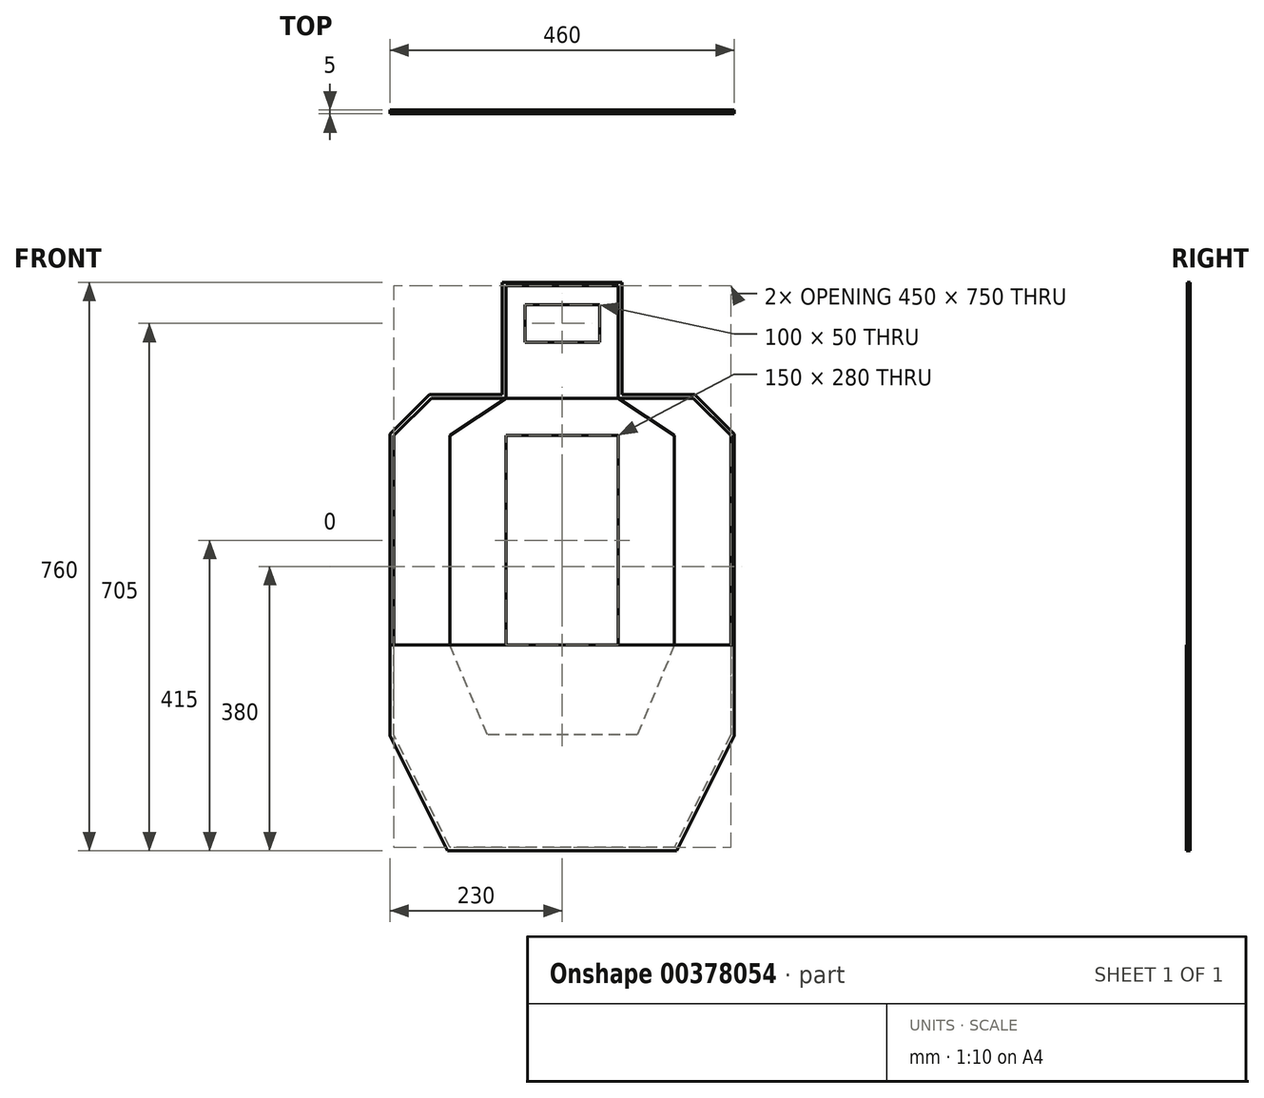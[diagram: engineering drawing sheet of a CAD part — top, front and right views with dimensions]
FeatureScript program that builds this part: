
annotation { "Feature Type Name" : "Feature", "Feature Type Description" : "" }
export const myFeature = defineFeature(function(context is Context, id is Id, definition is map)
    precondition{}
    {
        {
            var Q0;
            Q0=qCreatedBy(makeId("Front.planeOp"),FACE);
            var sketch = newSketch(context, id + "F0", { "sketchPlane" : qUnion([Q0])});
            skLineSegment(sketch, "E0.bottom", {"start": v(0, 100) * mm, "end": v(50, 100) * mm, "construction": true});
            skLineSegment(sketch, "E0.top", {"start": v(0, 125) * mm, "end": v(50, 125) * mm});
            skLineSegment(sketch, "E0.right", {"start": v(50, 100) * mm, "end": v(50, 125) * mm});
            skLineSegment(sketch, "E1.MirrorCS", {"start": v(0, 75) * mm, "end": v(50, 75) * mm});
            skLineSegment(sketch, "E2.MirrorCS", {"start": v(50, 100) * mm, "end": v(50, 75) * mm});
            skLineSegment(sketch, "E3.MirrorCS", {"start": v(0, 0) * mm, "end": v(0, 100) * mm, "construction": true});
            skLineSegment(sketch, "E4.MirrorCS", {"start": v(0, 125) * mm, "end": v(-50, 125) * mm});
            skLineSegment(sketch, "E5.MirrorCS", {"start": v(-50, 100) * mm, "end": v(-50, 125) * mm});
            skLineSegment(sketch, "E6.MirrorCS", {"start": v(-50, 100) * mm, "end": v(-50, 75) * mm});
            skLineSegment(sketch, "E7.MirrorCS", {"start": v(0, 75) * mm, "end": v(-50, 75) * mm});
            skSolve(sketch);
        }
        {
            var Q0;
            Q0=qSketchRegion(id+"F0",true);
            extrude(context, id + "F1", {"entities" : qUnion([Q0]), "oppositeDirection" : true, "depth" : 3 * mm});
        }
        {
            var Q0;
            Q0=qCreatedBy(makeId("Front.planeOp"),FACE);
            var sketch = newSketch(context, id + "F2", { "sketchPlane" : qUnion([Q0])});
            skLineSegment(sketch, "E8", {"start": v(75, 0) * mm, "end": v(75, 150) * mm});
            skLineSegment(sketch, "E9", {"start": v(75, 150) * mm, "end": v(-75, 150) * mm});
            skLineSegment(sketch, "E10", {"start": v(-75, 150) * mm, "end": v(-75, 0) * mm});
            skLineSegment(sketch, "E11", {"start": v(-75, 0) * mm, "end": v(75, 0) * mm});
            skLineSegment(sketch, "E12.0", {"start": v(0, 125) * mm, "end": v(-50, 125) * mm});
            skLineSegment(sketch, "E13.0", {"start": v(0, 125) * mm, "end": v(50, 125) * mm});
            skLineSegment(sketch, "E14.0", {"start": v(50, 100) * mm, "end": v(50, 125) * mm});
            skLineSegment(sketch, "E15.1", {"start": v(50, 100) * mm, "end": v(50, 75) * mm});
            skLineSegment(sketch, "E16.0", {"start": v(0, 75) * mm, "end": v(50, 75) * mm});
            skLineSegment(sketch, "E17.0", {"start": v(0, 75) * mm, "end": v(-50, 75) * mm});
            skLineSegment(sketch, "E18.0", {"start": v(-50, 100) * mm, "end": v(-50, 75) * mm});
            skLineSegment(sketch, "E19.1", {"start": v(-50, 100) * mm, "end": v(-50, 125) * mm});
            skLineSegment(sketch, "E20", {"start": v(0, 125) * mm, "end": v(0, 150) * mm, "construction": true});
            skLineSegment(sketch, "E21", {"start": v(0, 150) * mm, "end": v(0, 137.5) * mm, "construction": true});
            skSolve(sketch);
        }
        {
            var Q0;
            {var subQ0=sQuery(id+"F2.wireOp",EDGE,"E8");Q0=makeQuery(id+"F2.imprint","IMPRINT",FACE,{"disambiguationData":[TD([[makeQuery(id+"F2.imprint","IMPRINT",EDGE,{"derivedFrom":subQ0}),1.0]])]});}
            extrude(context, id + "F3", {"entities" : qUnion([Q0]), "oppositeDirection" : true, "depth" : 3 * mm});
        }
        {
            var Q0;
            Q0=qCreatedBy(makeId("Front.planeOp"),FACE);
            var sketch = newSketch(context, id + "F4", { "sketchPlane" : qUnion([Q0])});
            skLineSegment(sketch, "E22.bottom", {"start": v(75, -50) * mm, "end": v(-75, -50) * mm});
            skLineSegment(sketch, "E22.top", {"start": v(75, -330) * mm, "end": v(-75, -330) * mm});
            skLineSegment(sketch, "E22.left", {"start": v(75, -50) * mm, "end": v(75, -330) * mm});
            skLineSegment(sketch, "E22.right", {"start": v(-75, -50) * mm, "end": v(-75, -330) * mm});
            skLineSegment(sketch, "E23", {"start": v(0, 0) * mm, "end": v(0, -50) * mm, "construction": true});
            skLineSegment(sketch, "E24.0", {"start": v(-75, 0) * mm, "end": v(75, 0) * mm, "construction": true});
            skLineSegment(sketch, "E25", {"start": v(75, 0) * mm, "end": v(75, -50) * mm, "construction": true});
            skSolve(sketch);
        }
        {
            var Q0;
            Q0=makeQuery(id+"F4.imprint","IMPRINT",FACE,{"disambiguationData":[TD([[makeQuery(id+"F4.imprint","IMPRINT",EDGE,{"derivedFrom":sQuery(id+"F4.wireOp",EDGE,"E22.bottom")}),1.0]])]});
            extrude(context, id + "F5", {"entities" : qUnion([Q0]), "oppositeDirection" : true, "depth" : 3 * mm});
        }
        {
            var Q0;
            Q0=qCreatedBy(makeId("Front.planeOp"),FACE);
            var sketch = newSketch(context, id + "F6", { "sketchPlane" : qUnion([Q0])});
            skLineSegment(sketch, "E26.0", {"start": v(-75, 0) * mm, "end": v(75, 0) * mm});
            skLineSegment(sketch, "E27.1", {"start": v(75, -50) * mm, "end": v(75, -330) * mm});
            skLineSegment(sketch, "E28.2", {"start": v(75, -50) * mm, "end": v(-75, -50) * mm});
            skLineSegment(sketch, "E29.3", {"start": v(-75, -50) * mm, "end": v(-75, -330) * mm});
            skLineSegment(sketch, "E30.0", {"start": v(75, -330) * mm, "end": v(-75, -330) * mm});
            skLineSegment(sketch, "E31", {"start": v(75, 0) * mm, "end": v(150, -50) * mm});
            skLineSegment(sketch, "E32", {"start": v(150, -50) * mm, "end": v(150, -330) * mm});
            skLineSegment(sketch, "E33", {"start": v(150, -330) * mm, "end": v(100, -450) * mm});
            skLineSegment(sketch, "E34", {"start": v(100, -450) * mm, "end": v(-100, -450) * mm});
            skLineSegment(sketch, "E35", {"start": v(-100, -450) * mm, "end": v(-150, -330) * mm});
            skLineSegment(sketch, "E36", {"start": v(-150, -330) * mm, "end": v(-150, -50) * mm});
            skLineSegment(sketch, "E37", {"start": v(-150, -50) * mm, "end": v(-75, 0) * mm});
            skLineSegment(sketch, "E38", {"start": v(0, -450) * mm, "end": v(0, -50) * mm, "construction": true});
            skLineSegment(sketch, "E39", {"start": v(150, -50) * mm, "end": v(75, -50) * mm, "construction": true});
            skLineSegment(sketch, "E40", {"start": v(-55.04, -50) * mm, "end": v(-150, -50) * mm, "construction": true});
            skLineSegment(sketch, "E41", {"start": v(150, -330) * mm, "end": v(150, -450) * mm, "construction": true});
            skLineSegment(sketch, "E42", {"start": v(100, -450) * mm, "end": v(150, -450) * mm, "construction": true});
            skLineSegment(sketch, "E43", {"start": v(150, -330) * mm, "end": v(-150, -330) * mm, "construction": true});
            skLineSegment(sketch, "E44", {"start": v(-150, -330) * mm, "end": v(-150, -450) * mm, "construction": true});
            skLineSegment(sketch, "E45", {"start": v(-150, -450) * mm, "end": v(-100, -450) * mm, "construction": true});
            skSolve(sketch);
        }
        {
            var Q0;
            Q0=makeQuery(id+"F6.imprint","IMPRINT",FACE,{"disambiguationData":[TD([[makeQuery(id+"F6.imprint","IMPRINT",EDGE,{"derivedFrom":sQuery(id+"F6.wireOp",EDGE,"E26.0")}),-1.0]])]});
            extrude(context, id + "F7", {"entities" : qUnion([Q0]), "oppositeDirection" : true, "depth" : 3 * mm});
        }
        {
            var Q0;
            Q0=makeQuery(id+"F7.opExtrude","CAP_FACE",FACE,{"disambiguationData":[OSD([sQuery(id+"F6.wireOp",EDGE,"E26.0"),sQuery(id+"F6.wireOp",EDGE,"E27.1"),sQuery(id+"F6.wireOp",EDGE,"E28.2"),sQuery(id+"F6.wireOp",EDGE,"E29.3"),sQuery(id+"F6.wireOp",EDGE,"E30.0"),sQuery(id+"F6.wireOp",EDGE,"E31"),sQuery(id+"F6.wireOp",EDGE,"E32"),sQuery(id+"F6.wireOp",EDGE,"E33"),sQuery(id+"F6.wireOp",EDGE,"E34"),sQuery(id+"F6.wireOp",EDGE,"E35"),sQuery(id+"F6.wireOp",EDGE,"E36"),sQuery(id+"F6.wireOp",EDGE,"E37")])],"isStart":true});
            var sketch = newSketch(context, id + "F8", { "sketchPlane" : qUnion([Q0])});
            skLineSegment(sketch, "E46.0", {"start": v(75, 0) * mm, "end": v(150, -50) * mm});
            skLineSegment(sketch, "E47.0", {"start": v(150, -50) * mm, "end": v(150, -330) * mm});
            skLineSegment(sketch, "E48.0", {"start": v(150, -330) * mm, "end": v(100, -450) * mm});
            skLineSegment(sketch, "E49.1", {"start": v(100, -450) * mm, "end": v(-100, -450) * mm});
            skLineSegment(sketch, "E50.0", {"start": v(-150, -330) * mm, "end": v(-150, -50) * mm});
            skLineSegment(sketch, "E51.0", {"start": v(-100, -450) * mm, "end": v(-150, -330) * mm});
            skLineSegment(sketch, "E52.0", {"start": v(-150, -50) * mm, "end": v(-75, 0) * mm});
            skLineSegment(sketch, "E53", {"start": v(75, 0) * mm, "end": v(175, 0) * mm});
            skLineSegment(sketch, "E54", {"start": v(175, 0) * mm, "end": v(225, -50) * mm});
            skLineSegment(sketch, "E55", {"start": v(225, -50) * mm, "end": v(225, -450) * mm});
            skLineSegment(sketch, "E56", {"start": v(225, -450) * mm, "end": v(150, -600) * mm});
            skLineSegment(sketch, "E57", {"start": v(150, -600) * mm, "end": v(-150, -600) * mm});
            skLineSegment(sketch, "E58", {"start": v(-150, -600) * mm, "end": v(-225, -450) * mm});
            skLineSegment(sketch, "E59", {"start": v(-225, -450) * mm, "end": v(-225, -50) * mm});
            skLineSegment(sketch, "E60", {"start": v(-225, -50) * mm, "end": v(-175, 0) * mm});
            skLineSegment(sketch, "E61", {"start": v(-175, 0) * mm, "end": v(-75, 0) * mm});
            skLineSegment(sketch, "E62", {"start": v(225, -50) * mm, "end": v(225, 0) * mm, "construction": true});
            skLineSegment(sketch, "E63", {"start": v(225, 0) * mm, "end": v(175, 0) * mm, "construction": true});
            skLineSegment(sketch, "E64", {"start": v(225, -450) * mm, "end": v(225, -600) * mm, "construction": true});
            skLineSegment(sketch, "E65", {"start": v(225, -600) * mm, "end": v(150, -600) * mm, "construction": true});
            skLineSegment(sketch, "E66", {"start": v(-225, -450) * mm, "end": v(-225, -600) * mm, "construction": true});
            skLineSegment(sketch, "E67", {"start": v(-225, -600) * mm, "end": v(-150, -600) * mm, "construction": true});
            skLineSegment(sketch, "E68", {"start": v(-175, 0) * mm, "end": v(-225, 0) * mm, "construction": true});
            skLineSegment(sketch, "E69", {"start": v(-225, 0) * mm, "end": v(-225, -50) * mm, "construction": true});
            skSolve(sketch);
        }
        {
            var Q0;
            Q0=qSketchRegion(id+"F8",true);
            extrude(context, id + "F9", {"entities" : qUnion([Q0]), "oppositeDirection" : true, "depth" : 3 * mm});
        }
        {
            var Q0;
            Q0=makeQuery(id+"F9.opExtrude","CAP_FACE",FACE,{"disambiguationData":[OSD([sQuery(id+"F8.wireOp",EDGE,"E46.0"),sQuery(id+"F8.wireOp",EDGE,"E47.0"),sQuery(id+"F8.wireOp",EDGE,"E48.0"),sQuery(id+"F8.wireOp",EDGE,"E49.1"),sQuery(id+"F8.wireOp",EDGE,"E50.0"),sQuery(id+"F8.wireOp",EDGE,"E51.0"),sQuery(id+"F8.wireOp",EDGE,"E52.0"),sQuery(id+"F8.wireOp",EDGE,"E53"),sQuery(id+"F8.wireOp",EDGE,"E54"),sQuery(id+"F8.wireOp",EDGE,"E55"),sQuery(id+"F8.wireOp",EDGE,"E56"),sQuery(id+"F8.wireOp",EDGE,"E57"),sQuery(id+"F8.wireOp",EDGE,"E58"),sQuery(id+"F8.wireOp",EDGE,"E59"),sQuery(id+"F8.wireOp",EDGE,"E60"),sQuery(id+"F8.wireOp",EDGE,"E61")])],"isStart":true});
            var sketch = newSketch(context, id + "F10", { "sketchPlane" : qUnion([Q0])});
            skLineSegment(sketch, "E70.0", {"start": v(75, 150) * mm, "end": v(-75, 150) * mm});
            skLineSegment(sketch, "E71.0", {"start": v(75, 0) * mm, "end": v(75, 150) * mm});
            skLineSegment(sketch, "E72.1", {"start": v(75, 0) * mm, "end": v(175, 0) * mm});
            skLineSegment(sketch, "E73.0", {"start": v(175, 0) * mm, "end": v(225, -50) * mm});
            skLineSegment(sketch, "E74.1", {"start": v(225, -50) * mm, "end": v(225, -450) * mm});
            skLineSegment(sketch, "E75.0", {"start": v(225, -450) * mm, "end": v(150, -600) * mm});
            skLineSegment(sketch, "E76.1", {"start": v(150, -600) * mm, "end": v(-150, -600) * mm});
            skLineSegment(sketch, "E77.2", {"start": v(-150, -600) * mm, "end": v(-225, -450) * mm});
            skLineSegment(sketch, "E78.3", {"start": v(-225, -450) * mm, "end": v(-225, -50) * mm});
            skLineSegment(sketch, "E79.4", {"start": v(-225, -50) * mm, "end": v(-175, 0) * mm});
            skLineSegment(sketch, "E80.5", {"start": v(-175, 0) * mm, "end": v(-75, 0) * mm});
            skLineSegment(sketch, "E81.0", {"start": v(-75, 150) * mm, "end": v(-75, 0) * mm});
            skLineSegment(sketch, "E82.0", {"start": v(177.07, 5) * mm, "end": v(230, -47.93) * mm});
            skLineSegment(sketch, "E82.1", {"start": v(-230, -451.18) * mm, "end": v(-230, -47.93) * mm});
            skLineSegment(sketch, "E82.2", {"start": v(-153.1, -605) * mm, "end": v(-230, -451.18) * mm});
            skLineSegment(sketch, "E82.3", {"start": v(153.1, -605) * mm, "end": v(-153.1, -605) * mm});
            skLineSegment(sketch, "E82.4", {"start": v(230, -451.18) * mm, "end": v(153.1, -605) * mm});
            skLineSegment(sketch, "E82.5", {"start": v(-230, -47.93) * mm, "end": v(-177.07, 5) * mm});
            skLineSegment(sketch, "E82.6", {"start": v(230, -47.93) * mm, "end": v(230, -451.18) * mm});
            skLineSegment(sketch, "E82.7", {"start": v(-177.07, 5) * mm, "end": v(-80, 5) * mm});
            skLineSegment(sketch, "E82.8", {"start": v(-80, 155) * mm, "end": v(-80, 5) * mm});
            skLineSegment(sketch, "E82.9", {"start": v(80, 155) * mm, "end": v(-80, 155) * mm});
            skLineSegment(sketch, "E82.10", {"start": v(80, 5) * mm, "end": v(80, 155) * mm});
            skLineSegment(sketch, "E82.11", {"start": v(80, 5) * mm, "end": v(177.07, 5) * mm});
            skSolve(sketch);
        }
        {
            var Q0;
            Q0=makeQuery(id+"F10.imprint","IMPRINT",FACE,{"disambiguationData":[TD([[makeQuery(id+"F10.imprint","IMPRINT",EDGE,{"derivedFrom":sQuery(id+"F10.wireOp",EDGE,"E70.0")}),-1.0]])]});
            extrude(context, id + "F11", {"entities" : qUnion([Q0]), "oppositeDirection" : true, "depth" : 3 * mm});
        }
        {
            var Q0;
            Q0=makeQuery(id+"F9.opExtrude","CAP_FACE",FACE,{"disambiguationData":[OSD([sQuery(id+"F8.wireOp",EDGE,"E46.0"),sQuery(id+"F8.wireOp",EDGE,"E47.0"),sQuery(id+"F8.wireOp",EDGE,"E48.0"),sQuery(id+"F8.wireOp",EDGE,"E49.1"),sQuery(id+"F8.wireOp",EDGE,"E50.0"),sQuery(id+"F8.wireOp",EDGE,"E51.0"),sQuery(id+"F8.wireOp",EDGE,"E52.0"),sQuery(id+"F8.wireOp",EDGE,"E53"),sQuery(id+"F8.wireOp",EDGE,"E54"),sQuery(id+"F8.wireOp",EDGE,"E55"),sQuery(id+"F8.wireOp",EDGE,"E56"),sQuery(id+"F8.wireOp",EDGE,"E57"),sQuery(id+"F8.wireOp",EDGE,"E58"),sQuery(id+"F8.wireOp",EDGE,"E59"),sQuery(id+"F8.wireOp",EDGE,"E60"),sQuery(id+"F8.wireOp",EDGE,"E61")])],"isStart":false});
            var sketch = newSketch(context, id + "F12", { "sketchPlane" : qUnion([Q0])});
            skLineSegment(sketch, "E83.0", {"start": v(75, 150) * mm, "end": v(75, 0) * mm});
            skLineSegment(sketch, "E84.0", {"start": v(175, 0) * mm, "end": v(75, 0) * mm});
            skLineSegment(sketch, "E85.0", {"start": v(-75, 150) * mm, "end": v(75, 150) * mm});
            skLineSegment(sketch, "E86.0", {"start": v(225, -50) * mm, "end": v(175, 0) * mm});
            skLineSegment(sketch, "E87.0", {"start": v(-225, -50) * mm, "end": v(-225, -450) * mm});
            skLineSegment(sketch, "E87.1", {"start": v(225, -450) * mm, "end": v(225, -50) * mm});
            skLineSegment(sketch, "E87.2", {"start": v(150, -600) * mm, "end": v(225, -450) * mm});
            skLineSegment(sketch, "E87.3", {"start": v(-225, -450) * mm, "end": v(-150, -600) * mm});
            skLineSegment(sketch, "E87.4", {"start": v(-150, -600) * mm, "end": v(150, -600) * mm});
            skLineSegment(sketch, "E88.0", {"start": v(-175, 0) * mm, "end": v(-225, -50) * mm});
            skLineSegment(sketch, "E89.0", {"start": v(-75, 0) * mm, "end": v(-175, 0) * mm});
            skLineSegment(sketch, "E90.0", {"start": v(-75, 0) * mm, "end": v(-75, 150) * mm});
            skSolve(sketch);
        }
        {
            var Q0;
            Q0=qSketchRegion(id+"F12",true);
            extrude(context, id + "F13", {"entities" : qUnion([Q0]), "depth" : 1 * mm});
        }
        {
            var Q0;
            Q0=makeQuery(id+"F13.opExtrude","CAP_FACE",FACE,{"disambiguationData":[OSD([sQuery(id+"F12.wireOp",EDGE,"E83.0"),sQuery(id+"F12.wireOp",EDGE,"E84.0"),sQuery(id+"F12.wireOp",EDGE,"E85.0"),sQuery(id+"F12.wireOp",EDGE,"E86.0"),sQuery(id+"F12.wireOp",EDGE,"E87.0"),sQuery(id+"F12.wireOp",EDGE,"E87.1"),sQuery(id+"F12.wireOp",EDGE,"E87.2"),sQuery(id+"F12.wireOp",EDGE,"E87.3"),sQuery(id+"F12.wireOp",EDGE,"E87.4"),sQuery(id+"F12.wireOp",EDGE,"E88.0"),sQuery(id+"F12.wireOp",EDGE,"E89.0"),sQuery(id+"F12.wireOp",EDGE,"E90.0")])],"isStart":false});
            var sketch = newSketch(context, id + "F14", { "sketchPlane" : qUnion([Q0])});
            skLineSegment(sketch, "E91.0", {"start": v(-80, 155) * mm, "end": v(80, 155) * mm});
            skLineSegment(sketch, "E92.0", {"start": v(80, 155) * mm, "end": v(80, 5) * mm});
            skLineSegment(sketch, "E93.0", {"start": v(-80, 5) * mm, "end": v(-80, 155) * mm});
            skLineSegment(sketch, "E94.0", {"start": v(177.07, 5) * mm, "end": v(80, 5) * mm});
            skLineSegment(sketch, "E95.0", {"start": v(-80, 5) * mm, "end": v(-177.07, 5) * mm});
            skLineSegment(sketch, "E96.0", {"start": v(230, -47.93) * mm, "end": v(177.07, 5) * mm});
            skLineSegment(sketch, "E97.0", {"start": v(-177.07, 5) * mm, "end": v(-230, -47.93) * mm});
            skLineSegment(sketch, "E98.1", {"start": v(-230, -47.93) * mm, "end": v(-230, -451.18) * mm});
            skLineSegment(sketch, "E99.0", {"start": v(-230, -451.18) * mm, "end": v(-153.1, -605) * mm});
            skLineSegment(sketch, "E100.0", {"start": v(-153.1, -605) * mm, "end": v(153.1, -605) * mm});
            skLineSegment(sketch, "E101.0", {"start": v(153.1, -605) * mm, "end": v(230, -451.18) * mm});
            skLineSegment(sketch, "E102.0", {"start": v(230, -451.18) * mm, "end": v(230, -47.93) * mm});
            skLineSegment(sketch, "E103.0", {"start": v(-75, 150) * mm, "end": v(75, 150) * mm});
            skLineSegment(sketch, "E104.0", {"start": v(-75, 0) * mm, "end": v(-75, 150) * mm});
            skLineSegment(sketch, "E105.0", {"start": v(75, 150) * mm, "end": v(75, 0) * mm});
            skLineSegment(sketch, "E106.0", {"start": v(175, 0) * mm, "end": v(75, 0) * mm});
            skLineSegment(sketch, "E107.0", {"start": v(225, -50) * mm, "end": v(175, 0) * mm});
            skLineSegment(sketch, "E108.0", {"start": v(150, -600) * mm, "end": v(225, -450) * mm});
            skLineSegment(sketch, "E109.0", {"start": v(225, -450) * mm, "end": v(225, -50) * mm});
            skLineSegment(sketch, "E110.0", {"start": v(-150, -600) * mm, "end": v(150, -600) * mm});
            skLineSegment(sketch, "E111.0", {"start": v(-225, -450) * mm, "end": v(-150, -600) * mm});
            skLineSegment(sketch, "E112.0", {"start": v(-225, -50) * mm, "end": v(-225, -450) * mm});
            skLineSegment(sketch, "E113.0", {"start": v(-175, 0) * mm, "end": v(-225, -50) * mm});
            skLineSegment(sketch, "E114.0", {"start": v(-75, 0) * mm, "end": v(-175, 0) * mm});
            skSolve(sketch);
        }
        {
            var Q0;
            Q0=makeQuery(id+"F14.imprint","IMPRINT",FACE,{"disambiguationData":[TD([[makeQuery(id+"F14.imprint","IMPRINT",EDGE,{"derivedFrom":sQuery(id+"F14.wireOp",EDGE,"E91.0")}),-1.0]])]});
            extrude(context, id + "F15", {"entities" : qUnion([Q0]), "oppositeDirection" : true, "depth" : 1 * mm});
        }
        {
            var Q0;
            Q0=makeQuery(id+"F9.opExtrude","CAP_FACE",FACE,{"disambiguationData":[OSD([sQuery(id+"F8.wireOp",EDGE,"E46.0"),sQuery(id+"F8.wireOp",EDGE,"E47.0"),sQuery(id+"F8.wireOp",EDGE,"E48.0"),sQuery(id+"F8.wireOp",EDGE,"E49.1"),sQuery(id+"F8.wireOp",EDGE,"E50.0"),sQuery(id+"F8.wireOp",EDGE,"E51.0"),sQuery(id+"F8.wireOp",EDGE,"E52.0"),sQuery(id+"F8.wireOp",EDGE,"E53"),sQuery(id+"F8.wireOp",EDGE,"E54"),sQuery(id+"F8.wireOp",EDGE,"E55"),sQuery(id+"F8.wireOp",EDGE,"E56"),sQuery(id+"F8.wireOp",EDGE,"E57"),sQuery(id+"F8.wireOp",EDGE,"E58"),sQuery(id+"F8.wireOp",EDGE,"E59"),sQuery(id+"F8.wireOp",EDGE,"E60"),sQuery(id+"F8.wireOp",EDGE,"E61")])],"isStart":true});
            var sketch = newSketch(context, id + "F16", { "sketchPlane" : qUnion([Q0])});
            skLineSegment(sketch, "E115.0", {"start": v(-153.1, -605) * mm, "end": v(-230, -451.18) * mm});
            skLineSegment(sketch, "E116.0", {"start": v(-230, -451.18) * mm, "end": v(-230, -330) * mm});
            skLineSegment(sketch, "E117.0", {"start": v(153.1, -605) * mm, "end": v(-153.1, -605) * mm});
            skLineSegment(sketch, "E118.0", {"start": v(230, -451.18) * mm, "end": v(153.1, -605) * mm});
            skLineSegment(sketch, "E119.0", {"start": v(230, -330) * mm, "end": v(230, -451.18) * mm});
            skLineSegment(sketch, "E120.0", {"start": v(230, -330) * mm, "end": v(-230, -330) * mm});
            skPoint(sketch, "E121.orphan", {"position": v(75, -330) * mm});
            skPoint(sketch, "E122.orphan", {"position": v(-75, -330) * mm});
            skSolve(sketch);
        }
        {
            var Q0;
            Q0=qSketchRegion(id+"F16",true);
            extrude(context, id + "F17", {"entities" : qUnion([Q0]), "depth" : 1 * mm});
        }
    });
